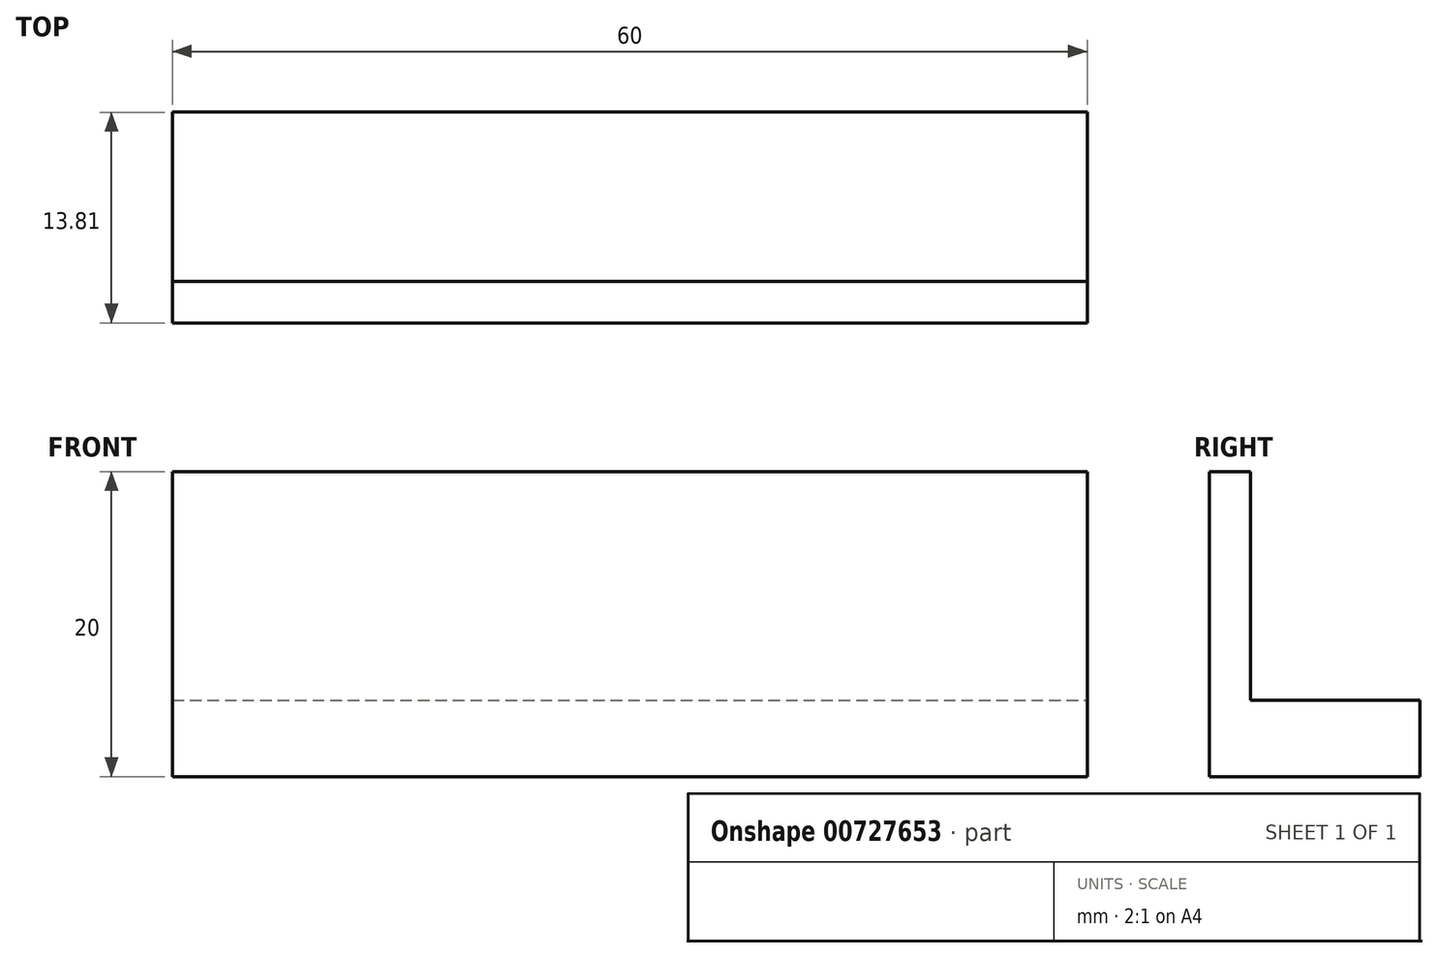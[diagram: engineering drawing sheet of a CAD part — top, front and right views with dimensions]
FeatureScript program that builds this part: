
annotation { "Feature Type Name" : "Feature", "Feature Type Description" : "" }
export const myFeature = defineFeature(function(context is Context, id is Id, definition is map)
    precondition{}
    {
        {
            var Q0;
            Q0=qCreatedBy(makeId("Top.planeOp"),FACE);
            var sketch = newSketch(context, id + "F0", { "sketchPlane" : qUnion([Q0])});
            skLineSegment(sketch, "E0", {"start": v(0, 0) * mm, "end": v(30, 0) * mm});
            skLineSegment(sketch, "E1", {"start": v(0, 0) * mm, "end": v(-30, 0) * mm});
            skLineSegment(sketch, "E2", {"start": v(-30, 0) * mm, "end": v(-30, 13.81) * mm});
            skLineSegment(sketch, "E3", {"start": v(-30, 13.81) * mm, "end": v(30, 13.81) * mm});
            skLineSegment(sketch, "E4", {"start": v(30, 13.81) * mm, "end": v(30, 0) * mm});
            skLineSegment(sketch, "E5", {"start": v(-30, 2.71) * mm, "end": v(30, 2.71) * mm});
            skPoint(sketch, "E6", {"position": v(-25.82, 11.75) * mm});
            skPoint(sketch, "E7", {"position": v(-17.82, 11.75) * mm});
            skPoint(sketch, "E8", {"position": v(-10.07, 11.75) * mm});
            skPoint(sketch, "E9", {"position": v(-3.1, 11.75) * mm});
            skPoint(sketch, "E10", {"position": v(5.16, 11.75) * mm});
            skPoint(sketch, "E11", {"position": v(11.62, 11.75) * mm});
            skPoint(sketch, "E12", {"position": v(19.1, 11.75) * mm});
            skPoint(sketch, "E13", {"position": v(25.3, 11.49) * mm});
            skSolve(sketch);
        }
        {
            var Q0;
            {var subQ4=sQuery(id+"F0.wireOp",EDGE,"E0");Q0=makeQuery(id+"F0.imprint","IMPRINT",FACE,{"disambiguationData":[TD([[makeQuery(id+"F0.imprint","IMPRINT",EDGE,{"derivedFrom":subQ4}),1.0]])]});}
            extrude(context, id + "F1", {"entities" : qUnion([Q0]), "depth" : 20 * mm, "offsetDistance" : 25 * mm});
        }
        {
            var Q0;
            Q0 = qSketchRegion(id + "F0", true);
            extrude(context, id + "F2", {"entities" : qUnion([Q0]), "operationType" : NewBodyOperationType.ADD, "depth" : 5 * mm, "offsetDistance" : 25 * mm});
        }
    });
